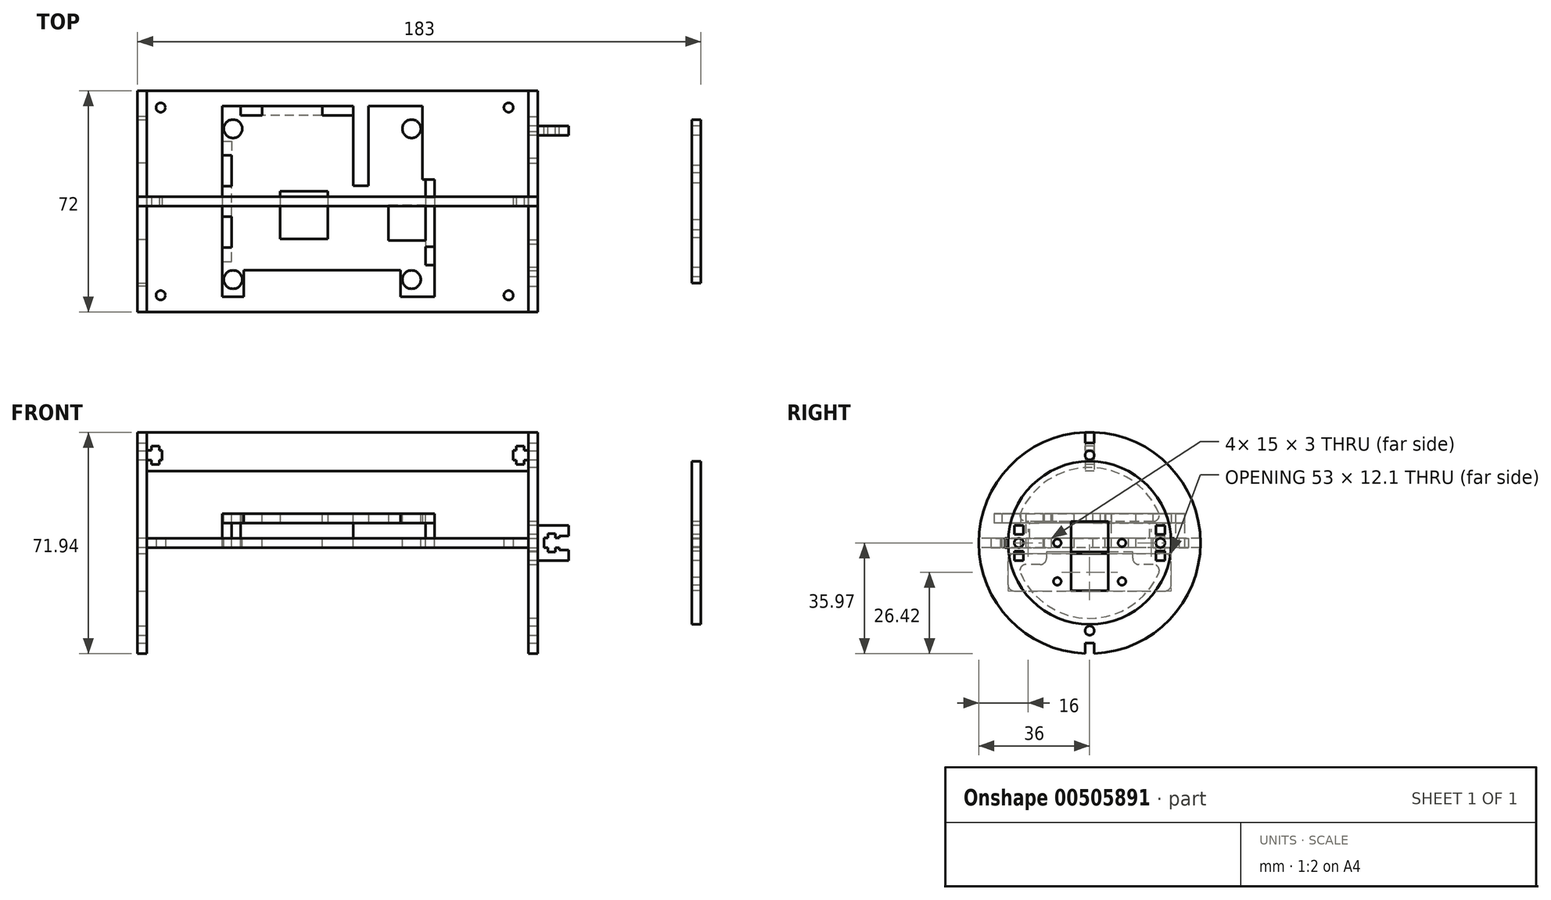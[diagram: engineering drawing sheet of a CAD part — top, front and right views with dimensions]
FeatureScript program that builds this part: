
annotation { "Feature Type Name" : "Feature", "Feature Type Description" : "" }
export const myFeature = defineFeature(function(context is Context, id is Id, definition is map)
    precondition{}
    {
        {
            var Q0;
            Q0=qCreatedBy(makeId("Top.planeOp"),FACE);
            var sketch = newSketch(context, id + "F0", { "sketchPlane" : qUnion([Q0])});
            skLineSegment(sketch, "E0.bottom", {"start": v(-62, 36) * mm, "end": v(62, 36) * mm});
            skLineSegment(sketch, "E0.top", {"start": v(-62, -36) * mm, "end": v(62, -36) * mm});
            skLineSegment(sketch, "E0.left", {"start": v(-62, 36) * mm, "end": v(-62, -36) * mm});
            skLineSegment(sketch, "E0.right", {"start": v(62, 36) * mm, "end": v(62, -36) * mm});
            skPoint(sketch, "E0.middle", {"position": v(0, 0) * mm});
            skLineSegment(sketch, "E1", {"start": v(0, 22.73) * mm, "end": v(0, 0) * mm, "construction": true});
            skLineSegment(sketch, "E2", {"start": v(0, 0) * mm, "end": v(28.2, 0) * mm, "construction": true});
            skLineSegment(sketch, "E3.bottom", {"start": v(62, 27.5) * mm, "end": v(65, 27.5) * mm});
            skLineSegment(sketch, "E3.top", {"start": v(62, 12.5) * mm, "end": v(65, 12.5) * mm});
            skLineSegment(sketch, "E3.left", {"start": v(62, 27.5) * mm, "end": v(62, 12.5) * mm});
            skLineSegment(sketch, "E3.right", {"start": v(65, 27.5) * mm, "end": v(65, 12.5) * mm});
            skPoint(sketch, "E3.middle", {"position": v(63.5, 20) * mm});
            skLineSegment(sketch, "E4.MirrorCS", {"start": v(-62, 27.5) * mm, "end": v(-65, 27.5) * mm});
            skLineSegment(sketch, "E5.MirrorCS", {"start": v(-65, 27.5) * mm, "end": v(-65, 12.5) * mm});
            skLineSegment(sketch, "E6.MirrorCS", {"start": v(-62, 12.5) * mm, "end": v(-65, 12.5) * mm});
            skLineSegment(sketch, "E7.MirrorCS", {"start": v(-62, -27.5) * mm, "end": v(-65, -27.5) * mm});
            skLineSegment(sketch, "E8.MirrorCS", {"start": v(-65, -27.5) * mm, "end": v(-65, -12.5) * mm});
            skLineSegment(sketch, "E9.MirrorCS", {"start": v(-62, -12.5) * mm, "end": v(-65, -12.5) * mm});
            skLineSegment(sketch, "E10.MirrorCS", {"start": v(62, -27.5) * mm, "end": v(65, -27.5) * mm});
            skLineSegment(sketch, "E11.MirrorCS", {"start": v(65, -27.5) * mm, "end": v(65, -12.5) * mm});
            skLineSegment(sketch, "E12.MirrorCS", {"start": v(62, -12.5) * mm, "end": v(65, -12.5) * mm});
            skSolve(sketch);
        }
        {
            var Q0;
            Q0 = qSketchRegion(id + "F0", true);
            extrude(context, id + "F1", {"entities" : qUnion([Q0]), "depth" : 3 * mm});
        }
        {
            var Q0;
            Q0=makeQuery(id+"F1.opExtrude","CAP_FACE",FACE,{"disambiguationData":[OSD([sQuery(id+"F0.wireOp",EDGE,"E0.bottom"),sQuery(id+"F0.wireOp",EDGE,"E0.top"),sQuery(id+"F0.wireOp",EDGE,"E0.left"),sQuery(id+"F0.wireOp",EDGE,"E0.right"),sQuery(id+"F0.wireOp",EDGE,"E3.bottom"),sQuery(id+"F0.wireOp",EDGE,"E3.top"),sQuery(id+"F0.wireOp",EDGE,"E3.right"),sQuery(id+"F0.wireOp",EDGE,"E4.MirrorCS"),sQuery(id+"F0.wireOp",EDGE,"E5.MirrorCS"),sQuery(id+"F0.wireOp",EDGE,"E6.MirrorCS"),sQuery(id+"F0.wireOp",EDGE,"E7.MirrorCS"),sQuery(id+"F0.wireOp",EDGE,"E8.MirrorCS"),sQuery(id+"F0.wireOp",EDGE,"E9.MirrorCS"),sQuery(id+"F0.wireOp",EDGE,"E10.MirrorCS"),sQuery(id+"F0.wireOp",EDGE,"E11.MirrorCS"),sQuery(id+"F0.wireOp",EDGE,"E12.MirrorCS")])],"isStart":true});
            cPlane(context, id + "F2", {"entities" : qUnion([Q0]), "cplaneType" : CPlaneType.OFFSET, "offset" : 8 * mm, "oppositeDirection" : true, "width" : 150 * mm, "height" : 150 * mm});
        }
        {
            var Q0;
            Q0=qCreatedBy(id+"F2.planeOp",FACE);
            var sketch = newSketch(context, id + "F3", { "sketchPlane" : qUnion([Q0])});
            skLineSegment(sketch, "E13.bottom", {"start": v(-37.5, -31) * mm, "end": v(47.5, -31) * mm});
            skLineSegment(sketch, "E13.top", {"start": v(-37.5, 31) * mm, "end": v(47.5, 31) * mm});
            skLineSegment(sketch, "E13.left", {"start": v(-37.5, -31) * mm, "end": v(-37.5, 31) * mm});
            skLineSegment(sketch, "E13.right", {"start": v(47.5, -31) * mm, "end": v(47.5, 31) * mm});
            skPoint(sketch, "E13.middle", {"position": v(5, 0) * mm});
            skLineSegment(sketch, "E14", {"start": v(27.5, -31) * mm, "end": v(27.5, -7.1) * mm});
            skLineSegment(sketch, "E15", {"start": v(27.5, -7.1) * mm, "end": v(31.5, -7.1) * mm});
            skLineSegment(sketch, "E16", {"start": v(31.5, -7.1) * mm, "end": v(31.5, 31) * mm});
            skLineSegment(sketch, "E17.bottom", {"start": v(-18.75, -3.35) * mm, "end": v(-3.25, -3.35) * mm});
            skLineSegment(sketch, "E17.top", {"start": v(-18.75, 12.15) * mm, "end": v(-3.25, 12.15) * mm});
            skLineSegment(sketch, "E17.left", {"start": v(-18.75, -3.35) * mm, "end": v(-18.75, 12.15) * mm});
            skLineSegment(sketch, "E17.right", {"start": v(-3.25, -3.35) * mm, "end": v(-3.25, 12.15) * mm});
            skPoint(sketch, "E17.middle", {"position": v(-11, 4.4) * mm});
            skLineSegment(sketch, "E18.bottom", {"start": v(16.5, 1.15) * mm, "end": v(28.5, 1.15) * mm});
            skLineSegment(sketch, "E18.top", {"start": v(16.5, 12.65) * mm, "end": v(28.5, 12.65) * mm});
            skLineSegment(sketch, "E18.left", {"start": v(16.5, 1.15) * mm, "end": v(16.5, 12.65) * mm});
            skLineSegment(sketch, "E18.right", {"start": v(28.5, 1.15) * mm, "end": v(28.5, 12.65) * mm});
            skLineSegment(sketch, "E19", {"start": v(-37.5, -27.1) * mm, "end": v(47.5, -27.1) * mm, "construction": true});
            skLineSegment(sketch, "E20", {"start": v(-37.5, 28.9) * mm, "end": v(47.5, 28.9) * mm, "construction": true});
            skLineSegment(sketch, "E21", {"start": v(-30.55, 31) * mm, "end": v(-30.55, 22.4) * mm});
            skLineSegment(sketch, "E22", {"start": v(-30.55, 22.4) * mm, "end": v(20.45, 22.4) * mm});
            skLineSegment(sketch, "E23", {"start": v(20.45, 22.4) * mm, "end": v(20.45, 31) * mm});
            skLineSegment(sketch, "E24", {"start": v(5, -31) * mm, "end": v(5, -5.1) * mm});
            skLineSegment(sketch, "E25", {"start": v(5, -5.1) * mm, "end": v(10, -5.1) * mm});
            skLineSegment(sketch, "E26", {"start": v(10, -5.1) * mm, "end": v(10, -31) * mm});
            skCircle(sketch, "E27", {"center": v(-34, -23.6) * mm, "radius": 1.5 * mm});
            skCircle(sketch, "E28", {"center": v(24, -23.6) * mm, "radius": 1.5 * mm});
            skCircle(sketch, "E29", {"center": v(-34, 25.4) * mm, "radius": 1.5 * mm});
            skCircle(sketch, "E30", {"center": v(24, 25.4) * mm, "radius": 1.5 * mm});
            skSolve(sketch);
        }
        {
            var Q0;
            {var subQ6=sQuery(id+"F3.wireOp",EDGE,"E13.left");Q0=makeQuery(id+"F3.imprint","IMPRINT",FACE,{"disambiguationData":[TD([[makeQuery(id+"F3.imprint","IMPRINT",EDGE,{"derivedFrom":subQ6}),-1.0]])]});}
            extrude(context, id + "F4", {"entities" : qUnion([Q0]), "oppositeDirection" : true, "depth" : 3 * mm});
        }
        {
            var Q0;
            Q0=makeQuery(id+"F4.opExtrude","CAP_FACE",FACE,{"disambiguationData":[OSD([sQuery(id+"F3.wireOp",EDGE,"E13.bottom"),sQuery(id+"F3.wireOp",EDGE,"E13.top"),sQuery(id+"F3.wireOp",EDGE,"E13.left"),sQuery(id+"F3.wireOp",EDGE,"E14"),sQuery(id+"F3.wireOp",EDGE,"E15"),sQuery(id+"F3.wireOp",EDGE,"E16"),sQuery(id+"F3.wireOp",EDGE,"E17.bottom"),sQuery(id+"F3.wireOp",EDGE,"E17.top"),sQuery(id+"F3.wireOp",EDGE,"E17.left"),sQuery(id+"F3.wireOp",EDGE,"E17.right"),sQuery(id+"F3.wireOp",EDGE,"E18.bottom"),sQuery(id+"F3.wireOp",EDGE,"E18.top"),sQuery(id+"F3.wireOp",EDGE,"E18.left"),sQuery(id+"F3.wireOp",EDGE,"E18.right"),sQuery(id+"F3.wireOp",EDGE,"E21"),sQuery(id+"F3.wireOp",EDGE,"E22"),sQuery(id+"F3.wireOp",EDGE,"E23"),sQuery(id+"F3.wireOp",EDGE,"E24"),sQuery(id+"F3.wireOp",EDGE,"E25"),sQuery(id+"F3.wireOp",EDGE,"E26"),sQuery(id+"F3.wireOp",EDGE,"E27"),sQuery(id+"F3.wireOp",EDGE,"E28"),sQuery(id+"F3.wireOp",EDGE,"E29"),sQuery(id+"F3.wireOp",EDGE,"E30")])],"isStart":false});
            var sketch = newSketch(context, id + "F5", { "sketchPlane" : qUnion([Q0])});
            skLineSegment(sketch, "E31.bottom", {"start": v(31.5, -20.68) * mm, "end": v(28.5, -20.68) * mm});
            skLineSegment(sketch, "E31.top", {"start": v(31.5, -14.68) * mm, "end": v(28.5, -14.68) * mm});
            skLineSegment(sketch, "E31.left", {"start": v(31.5, -20.68) * mm, "end": v(31.5, -14.68) * mm});
            skLineSegment(sketch, "E31.right", {"start": v(28.5, -20.68) * mm, "end": v(28.5, -14.68) * mm});
            skPoint(sketch, "E31.middle", {"position": v(30, -17.68) * mm});
            skLineSegment(sketch, "E32.bottom", {"start": v(31.5, 7.1) * mm, "end": v(28.5, 7.1) * mm});
            skLineSegment(sketch, "E32.top", {"start": v(31.5, 1.1) * mm, "end": v(28.5, 1.1) * mm});
            skLineSegment(sketch, "E32.left", {"start": v(31.5, 7.1) * mm, "end": v(31.5, 1.1) * mm});
            skLineSegment(sketch, "E32.right", {"start": v(28.5, 7.1) * mm, "end": v(28.5, 1.1) * mm});
            skPoint(sketch, "E32.middle", {"position": v(30, 4.1) * mm});
            skLineSegment(sketch, "E33.bottom", {"start": v(5, 31) * mm, "end": v(-5, 31) * mm});
            skLineSegment(sketch, "E33.top", {"start": v(5, 28) * mm, "end": v(-5, 28) * mm});
            skLineSegment(sketch, "E33.left", {"start": v(5, 31) * mm, "end": v(5, 28) * mm});
            skLineSegment(sketch, "E33.right", {"start": v(-5, 31) * mm, "end": v(-5, 28) * mm});
            skPoint(sketch, "E33.middle", {"position": v(0, 29.5) * mm});
            skLineSegment(sketch, "E34.bottom", {"start": v(-24.5, 31) * mm, "end": v(-31.5, 31) * mm});
            skLineSegment(sketch, "E34.top", {"start": v(-24.5, 28) * mm, "end": v(-31.5, 28) * mm});
            skLineSegment(sketch, "E34.left", {"start": v(-24.5, 31) * mm, "end": v(-24.5, 28) * mm});
            skLineSegment(sketch, "E34.right", {"start": v(-31.5, 31) * mm, "end": v(-31.5, 28) * mm});
            skPoint(sketch, "E34.middle", {"position": v(-28, 29.5) * mm});
            skLineSegment(sketch, "E35.bottom", {"start": v(-37.5, -15) * mm, "end": v(-34.5, -15) * mm});
            skLineSegment(sketch, "E35.top", {"start": v(-37.5, -5) * mm, "end": v(-34.5, -5) * mm});
            skLineSegment(sketch, "E35.left", {"start": v(-37.5, -15) * mm, "end": v(-37.5, -5) * mm});
            skLineSegment(sketch, "E35.right", {"start": v(-34.5, -15) * mm, "end": v(-34.5, -5) * mm});
            skPoint(sketch, "E35.middle", {"position": v(-36, -10) * mm});
            skLineSegment(sketch, "E36.bottom", {"start": v(-37.5, 5) * mm, "end": v(-34.5, 5) * mm});
            skLineSegment(sketch, "E36.top", {"start": v(-37.5, 15) * mm, "end": v(-34.5, 15) * mm});
            skLineSegment(sketch, "E36.left", {"start": v(-37.5, 5) * mm, "end": v(-37.5, 15) * mm});
            skLineSegment(sketch, "E36.right", {"start": v(-34.5, 5) * mm, "end": v(-34.5, 15) * mm});
            skPoint(sketch, "E36.middle", {"position": v(-36, 10) * mm});
            skPoint(sketch, "E37", {"position": v(-37.5, 0) * mm});
            skCircle(sketch, "E38.0", {"center": v(24, -25.4) * mm, "radius": 1.5 * mm, "construction": true});
            skCircle(sketch, "E38.1", {"center": v(24, 23.6) * mm, "radius": 1.5 * mm, "construction": true});
            skCircle(sketch, "E38.2", {"center": v(-34, 23.6) * mm, "radius": 1.5 * mm, "construction": true});
            skCircle(sketch, "E38.3", {"center": v(-34, -25.4) * mm, "radius": 1.5 * mm, "construction": true});
            skCircle(sketch, "E39", {"center": v(24, -25.4) * mm, "radius": 3 * mm});
            skCircle(sketch, "E40", {"center": v(-34, -25.4) * mm, "radius": 3 * mm});
            skCircle(sketch, "E41", {"center": v(24, 23.6) * mm, "radius": 3 * mm});
            skCircle(sketch, "E42", {"center": v(-34, 23.6) * mm, "radius": 3 * mm});
            skSolve(sketch);
        }
        {
            var Q0;
            Q0=makeQuery(id+"F5.imprint","IMPRINT",FACE,{"disambiguationData":[TD([[makeQuery(id+"F5.imprint","IMPRINT",EDGE,{"derivedFrom":sQuery(id+"F5.wireOp",EDGE,"E31.bottom")}),-1.0]])]});
            var Q1;
            Q1=makeQuery(id+"F5.imprint","IMPRINT",FACE,{"disambiguationData":[TD([[makeQuery(id+"F5.imprint","IMPRINT",EDGE,{"derivedFrom":sQuery(id+"F5.wireOp",EDGE,"E32.bottom")}),-1.0]])]});
            var Q2;
            Q2=makeQuery(id+"F5.imprint","IMPRINT",FACE,{"disambiguationData":[TD([[makeQuery(id+"F5.imprint","IMPRINT",EDGE,{"derivedFrom":sQuery(id+"F5.wireOp",EDGE,"E33.bottom")}),-1.0]])]});
            var Q3;
            Q3=makeQuery(id+"F5.imprint","IMPRINT",FACE,{"disambiguationData":[TD([[makeQuery(id+"F5.imprint","IMPRINT",EDGE,{"derivedFrom":sQuery(id+"F5.wireOp",EDGE,"E34.bottom")}),-1.0]])]});
            var Q4;
            Q4=makeQuery(id+"F5.imprint","IMPRINT",FACE,{"disambiguationData":[TD([[makeQuery(id+"F5.imprint","IMPRINT",EDGE,{"derivedFrom":sQuery(id+"F5.wireOp",EDGE,"E36.bottom")}),1.0]])]});
            var Q5;
            Q5=makeQuery(id+"F5.imprint","IMPRINT",FACE,{"disambiguationData":[TD([[makeQuery(id+"F5.imprint","IMPRINT",EDGE,{"derivedFrom":sQuery(id+"F5.wireOp",EDGE,"E35.bottom")}),1.0]])]});
            extrude(context, id + "F6", {"entities" : qUnion([Q0, Q1, Q2, Q3, Q4, Q5]), "operationType" : NewBodyOperationType.REMOVE, "oppositeDirection" : true, "depth" : 25 * mm});
        }
        {
            var Q0;
            Q0=makeQuery(id+"F5.imprint","IMPRINT",FACE,{"disambiguationData":[TD([[makeQuery(id+"F5.imprint","IMPRINT",EDGE,{"derivedFrom":sQuery(id+"F5.wireOp",EDGE,"E39")}),1.0]])]});
            var Q1;
            Q1=makeQuery(id+"F5.imprint","IMPRINT",FACE,{"disambiguationData":[TD([[makeQuery(id+"F5.imprint","IMPRINT",EDGE,{"derivedFrom":makeQuery(id+"F4.opExtrude","CAP_EDGE",EDGE,{"disambiguationData":[OSD([sQuery(id+"F3.wireOp",EDGE,"E30")])],"isStart":false})}),-1.0]])]});
            var Q2;
            Q2=makeQuery(id+"F5.imprint","IMPRINT",FACE,{"disambiguationData":[TD([[makeQuery(id+"F5.imprint","IMPRINT",EDGE,{"derivedFrom":sQuery(id+"F5.wireOp",EDGE,"E40")}),1.0]])]});
            var Q3;
            Q3=makeQuery(id+"F5.imprint","IMPRINT",FACE,{"disambiguationData":[TD([[makeQuery(id+"F5.imprint","IMPRINT",EDGE,{"derivedFrom":makeQuery(id+"F4.opExtrude","CAP_EDGE",EDGE,{"disambiguationData":[OSD([sQuery(id+"F3.wireOp",EDGE,"E29")])],"isStart":false})}),-1.0]])]});
            var Q4;
            Q4=makeQuery(id+"F5.imprint","IMPRINT",FACE,{"disambiguationData":[TD([[makeQuery(id+"F5.imprint","IMPRINT",EDGE,{"derivedFrom":sQuery(id+"F5.wireOp",EDGE,"E41")}),1.0]])]});
            var Q5;
            Q5=makeQuery(id+"F5.imprint","IMPRINT",FACE,{"disambiguationData":[TD([[makeQuery(id+"F5.imprint","IMPRINT",EDGE,{"derivedFrom":makeQuery(id+"F4.opExtrude","CAP_EDGE",EDGE,{"disambiguationData":[OSD([sQuery(id+"F3.wireOp",EDGE,"E28")])],"isStart":false})}),-1.0]])]});
            var Q6;
            Q6=makeQuery(id+"F5.imprint","IMPRINT",FACE,{"disambiguationData":[TD([[makeQuery(id+"F5.imprint","IMPRINT",EDGE,{"derivedFrom":sQuery(id+"F5.wireOp",EDGE,"E42")}),1.0]])]});
            var Q7;
            Q7=makeQuery(id+"F5.imprint","IMPRINT",FACE,{"disambiguationData":[TD([[makeQuery(id+"F5.imprint","IMPRINT",EDGE,{"derivedFrom":makeQuery(id+"F4.opExtrude","CAP_EDGE",EDGE,{"disambiguationData":[OSD([sQuery(id+"F3.wireOp",EDGE,"E27")])],"isStart":false})}),-1.0]])]});
            extrude(context, id + "F7", {"entities" : qUnion([Q0, Q1, Q2, Q3, Q4, Q5, Q6, Q7]), "operationType" : NewBodyOperationType.REMOVE, "oppositeDirection" : true, "depth" : 25 * mm});
        }
        {
            var Q0;
            {var subQ0=sQuery(id+"F3.wireOp",EDGE,"E30");var subQ1=sQuery(id+"F3.wireOp",EDGE,"E29");var subQ2=sQuery(id+"F3.wireOp",EDGE,"E28");var subQ3=sQuery(id+"F3.wireOp",EDGE,"E27");var subQ4=sQuery(id+"F3.wireOp",EDGE,"E26");var subQ5=sQuery(id+"F3.wireOp",EDGE,"E25");var subQ6=sQuery(id+"F3.wireOp",EDGE,"E24");var subQ7=sQuery(id+"F3.wireOp",EDGE,"E23");var subQ8=sQuery(id+"F3.wireOp",EDGE,"E22");var subQ9=sQuery(id+"F3.wireOp",EDGE,"E21");var subQ10=sQuery(id+"F3.wireOp",EDGE,"E18.right");var subQ11=sQuery(id+"F3.wireOp",EDGE,"E18.left");var subQ12=sQuery(id+"F3.wireOp",EDGE,"E18.top");var subQ13=sQuery(id+"F3.wireOp",EDGE,"E18.bottom");var subQ14=sQuery(id+"F3.wireOp",EDGE,"E17.right");var subQ15=sQuery(id+"F3.wireOp",EDGE,"E17.left");var subQ16=sQuery(id+"F3.wireOp",EDGE,"E17.top");var subQ17=sQuery(id+"F3.wireOp",EDGE,"E17.bottom");var subQ18=sQuery(id+"F3.wireOp",EDGE,"E16");var subQ19=sQuery(id+"F3.wireOp",EDGE,"E15");var subQ20=sQuery(id+"F3.wireOp",EDGE,"E14");var subQ21=sQuery(id+"F3.wireOp",EDGE,"E13.left");var subQ22=sQuery(id+"F3.wireOp",EDGE,"E13.top");var subQ23=sQuery(id+"F3.wireOp",EDGE,"E13.bottom");Q0=makeQuery(id+"F6.boolean.opBoolean","COPY",FACE,{"disambiguationData":[TD([makeQuery(id+"F4.opExtrude","CAP_FACE",FACE,{"disambiguationData":[OSD([subQ23,subQ22,subQ21,subQ20,subQ19,subQ18,subQ17,subQ16,subQ15,subQ14,subQ13,subQ12,subQ11,subQ10,subQ9,subQ8,subQ7,subQ6,subQ5,subQ4,subQ3,subQ2,subQ1,subQ0])],"isStart":true})])],"derivedFrom":makeQuery(id+"F6.opExtrude","SWEPT_FACE",FACE,{"disambiguationData":[OSD([sQuery(id+"F5.wireOp",EDGE,"E35.right")])]})});}
            var sketch = newSketch(context, id + "F8", { "sketchPlane" : qUnion([Q0])});
            skLineSegment(sketch, "E43.0", {"start": v(15, 0) * mm, "end": v(15, 3) * mm});
            skLineSegment(sketch, "E43.1", {"start": v(15, 0) * mm, "end": v(5, 0) * mm});
            skLineSegment(sketch, "E43.2", {"start": v(5, 0) * mm, "end": v(5, 3) * mm});
            skLineSegment(sketch, "E43.3", {"start": v(5, 8) * mm, "end": v(5, 11) * mm});
            skLineSegment(sketch, "E43.4", {"start": v(15, 11) * mm, "end": v(5, 11) * mm});
            skLineSegment(sketch, "E43.5", {"start": v(15, 8) * mm, "end": v(15, 11) * mm});
            skLineSegment(sketch, "E43.6", {"start": v(-5, 0) * mm, "end": v(-5, 3) * mm});
            skLineSegment(sketch, "E43.7", {"start": v(-5, 8) * mm, "end": v(-5, 11) * mm});
            skLineSegment(sketch, "E43.8", {"start": v(-5, 11) * mm, "end": v(-15, 11) * mm});
            skLineSegment(sketch, "E43.9", {"start": v(-15, 8) * mm, "end": v(-15, 11) * mm});
            skLineSegment(sketch, "E43.10", {"start": v(-15, 0) * mm, "end": v(-15, 3) * mm});
            skLineSegment(sketch, "E43.11", {"start": v(-5, 0) * mm, "end": v(-15, 0) * mm});
            skLineSegment(sketch, "E44", {"start": v(5, 3) * mm, "end": v(-5, 3) * mm});
            skLineSegment(sketch, "E45", {"start": v(5, 8) * mm, "end": v(-5, 8) * mm});
            skLineSegment(sketch, "E46", {"start": v(15, 3) * mm, "end": v(19.5, 3) * mm});
            skLineSegment(sketch, "E47", {"start": v(19.5, 3) * mm, "end": v(19.5, 8) * mm});
            skLineSegment(sketch, "E48", {"start": v(19.5, 8) * mm, "end": v(15, 8) * mm});
            skLineSegment(sketch, "E49", {"start": v(-15, 3) * mm, "end": v(-19.5, 3) * mm});
            skLineSegment(sketch, "E50", {"start": v(-19.5, 3) * mm, "end": v(-19.5, 8) * mm});
            skLineSegment(sketch, "E51", {"start": v(-19.5, 8) * mm, "end": v(-15, 8) * mm});
            skSolve(sketch);
        }
        {
            var Q0;
            Q0 = qSketchRegion(id + "F8", true);
            extrude(context, id + "F9", {"entities" : qUnion([Q0]), "depth" : 3 * mm});
        }
        {
            var Q0;
            {var subQ6=sQuery(id+"F3.wireOp",EDGE,"E24");Q0=makeQuery(id+"F6.boolean.opBoolean","COPY",FACE,{"disambiguationData":[TD([makeQuery(id+"F4.opExtrude","SWEPT_FACE",FACE,{"disambiguationData":[OSD([subQ6])]})])],"derivedFrom":makeQuery(id+"F6.opExtrude","SWEPT_FACE",FACE,{"disambiguationData":[OSD([sQuery(id+"F5.wireOp",EDGE,"E33.top")])]})});}
            var sketch = newSketch(context, id + "F10", { "sketchPlane" : qUnion([Q0])});
            skLineSegment(sketch, "E52.0", {"start": v(-5, 11) * mm, "end": v(5, 11) * mm});
            skLineSegment(sketch, "E52.1", {"start": v(5, 8) * mm, "end": v(5, 11) * mm});
            skLineSegment(sketch, "E52.2", {"start": v(24.5, 8) * mm, "end": v(24.5, 11) * mm});
            skLineSegment(sketch, "E52.3", {"start": v(24.5, 11) * mm, "end": v(31.5, 11) * mm});
            skLineSegment(sketch, "E52.4", {"start": v(24.5, 0) * mm, "end": v(31.5, 0) * mm});
            skLineSegment(sketch, "E52.5", {"start": v(24.5, 0) * mm, "end": v(24.5, 3) * mm});
            skLineSegment(sketch, "E52.6", {"start": v(-5, 0) * mm, "end": v(5, 0) * mm});
            skLineSegment(sketch, "E52.7", {"start": v(5, 0) * mm, "end": v(5, 3) * mm});
            skLineSegment(sketch, "E53", {"start": v(-5, 11) * mm, "end": v(-5, 0) * mm});
            skLineSegment(sketch, "E54", {"start": v(31.5, 11) * mm, "end": v(31.5, 0) * mm});
            skLineSegment(sketch, "E55", {"start": v(24.5, 8) * mm, "end": v(5, 8) * mm});
            skLineSegment(sketch, "E56", {"start": v(5, 3) * mm, "end": v(24.5, 3) * mm});
            skSolve(sketch);
        }
        {
            var Q0;
            Q0 = qSketchRegion(id + "F10", true);
            extrude(context, id + "F11", {"entities" : qUnion([Q0]), "depth" : 3 * mm});
        }
        {
            var Q0;
            {var subQ19=sQuery(id+"F3.wireOp",EDGE,"E15");Q0=makeQuery(id+"F6.boolean.opBoolean","COPY",FACE,{"disambiguationData":[TD([makeQuery(id+"F4.opExtrude","SWEPT_FACE",FACE,{"disambiguationData":[OSD([subQ19])]})])],"derivedFrom":makeQuery(id+"F6.opExtrude","SWEPT_FACE",FACE,{"disambiguationData":[OSD([sQuery(id+"F5.wireOp",EDGE,"E32.right")])]})});}
            var sketch = newSketch(context, id + "F12", { "sketchPlane" : qUnion([Q0])});
            skLineSegment(sketch, "E57.0", {"start": v(7.1, 11) * mm, "end": v(1.1, 11) * mm});
            skLineSegment(sketch, "E57.1", {"start": v(1.1, 8) * mm, "end": v(1.1, 11) * mm});
            skLineSegment(sketch, "E57.2", {"start": v(-14.68, 8) * mm, "end": v(-14.68, 11) * mm});
            skLineSegment(sketch, "E57.3", {"start": v(-20.68, 11) * mm, "end": v(-14.68, 11) * mm});
            skLineSegment(sketch, "E57.4", {"start": v(-20.68, 0) * mm, "end": v(-14.68, 0) * mm});
            skLineSegment(sketch, "E57.5", {"start": v(-14.68, 0) * mm, "end": v(-14.68, 3) * mm});
            skLineSegment(sketch, "E57.6", {"start": v(7.1, 0) * mm, "end": v(1.1, 0) * mm});
            skLineSegment(sketch, "E57.7", {"start": v(1.1, 0) * mm, "end": v(1.1, 3) * mm});
            skLineSegment(sketch, "E58", {"start": v(1.1, 3) * mm, "end": v(-14.68, 3) * mm});
            skLineSegment(sketch, "E59", {"start": v(1.1, 8) * mm, "end": v(-14.68, 8) * mm});
            skLineSegment(sketch, "E60", {"start": v(7.1, 0) * mm, "end": v(7.1, 11) * mm});
            skLineSegment(sketch, "E61", {"start": v(-20.68, 0) * mm, "end": v(-20.68, 11) * mm});
            skSolve(sketch);
        }
        {
            var Q0;
            Q0 = qSketchRegion(id + "F12", true);
            extrude(context, id + "F13", {"entities" : qUnion([Q0]), "depth" : 3 * mm});
        }
        {
            var Q0;
            {var subQ0=sQuery(id+"F0.wireOp",EDGE,"E0.right");Q0=makeQuery(id+"F1.opExtrude","SWEPT_FACE",FACE,{"disambiguationData":[OSD([subQ0]),TDD([makeQuery(id+"F0.imprint","IMPRINT",EDGE,{"disambiguationData":[TD([[makeQuery(id+"F0.imprint","INTERSECT",VERTEX,{"derivedFrom":[subQ0,sQuery(id+"F0.wireOp",EDGE,"E12.MirrorCS")]}),1.0]])],"derivedFrom":subQ0})])]});}
            var sketch = newSketch(context, id + "F14", { "sketchPlane" : qUnion([Q0])});
            skLineSegment(sketch, "E62", {"start": v(0, 0) * mm, "end": v(0, 3) * mm, "construction": true});
            skPoint(sketch, "E63", {"position": v(0, 1.5) * mm});
            skCircle(sketch, "E64", {"center": v(0, 1.5) * mm, "radius": 36 * mm});
            skCircle(sketch, "E65", {"center": v(0, 1.5) * mm, "radius": 24.5 * mm});
            skLineSegment(sketch, "E66", {"start": v(23.48, -5.5) * mm, "end": v(-23.48, -5.5) * mm});
            skLineSegment(sketch, "E67", {"start": v(23.48, 8.5) * mm, "end": v(-23.48, 8.5) * mm});
            skLineSegment(sketch, "E68", {"start": v(0, 1.5) * mm, "end": v(0, -10.66) * mm, "construction": true});
            skLineSegment(sketch, "E69", {"start": v(0, 1.5) * mm, "end": v(-8.88, 1.5) * mm, "construction": true});
            skLineSegment(sketch, "E70.bottom", {"start": v(24.5, -4.25) * mm, "end": v(21.5, -4.25) * mm});
            skLineSegment(sketch, "E70.top", {"start": v(24.5, -1.25) * mm, "end": v(21.5, -1.25) * mm});
            skLineSegment(sketch, "E70.left", {"start": v(24.5, -4.25) * mm, "end": v(24.5, -1.25) * mm});
            skLineSegment(sketch, "E70.right", {"start": v(21.5, -4.25) * mm, "end": v(21.5, -1.25) * mm});
            skPoint(sketch, "E70.middle", {"position": v(23, -2.75) * mm});
            skLineSegment(sketch, "E71.MirrorCS", {"start": v(21.5, 7.25) * mm, "end": v(21.5, 4.25) * mm});
            skLineSegment(sketch, "E72.MirrorCS", {"start": v(24.5, 7.25) * mm, "end": v(21.5, 7.25) * mm});
            skLineSegment(sketch, "E73.MirrorCS", {"start": v(24.5, 7.25) * mm, "end": v(24.5, 4.25) * mm});
            skLineSegment(sketch, "E74.MirrorCS", {"start": v(24.5, 4.25) * mm, "end": v(21.5, 4.25) * mm});
            skPoint(sketch, "E75.MirrorP", {"position": v(23, 5.75) * mm});
            skLineSegment(sketch, "E76.MirrorCS", {"start": v(-21.5, -4.25) * mm, "end": v(-21.5, -1.25) * mm});
            skLineSegment(sketch, "E77.MirrorCS", {"start": v(-24.5, -4.25) * mm, "end": v(-21.5, -4.25) * mm});
            skLineSegment(sketch, "E78.MirrorCS", {"start": v(-24.5, -4.25) * mm, "end": v(-24.5, -1.25) * mm});
            skLineSegment(sketch, "E79.MirrorCS", {"start": v(-24.5, -1.25) * mm, "end": v(-21.5, -1.25) * mm});
            skLineSegment(sketch, "E80.MirrorCS", {"start": v(-24.5, 4.25) * mm, "end": v(-21.5, 4.25) * mm});
            skLineSegment(sketch, "E81.MirrorCS", {"start": v(-21.5, 7.25) * mm, "end": v(-21.5, 4.25) * mm});
            skLineSegment(sketch, "E82.MirrorCS", {"start": v(-24.5, 7.25) * mm, "end": v(-21.5, 7.25) * mm});
            skLineSegment(sketch, "E83.MirrorCS", {"start": v(-24.5, 7.25) * mm, "end": v(-24.5, 4.25) * mm});
            skLineSegment(sketch, "E84", {"start": v(14, -5.5) * mm, "end": v(14, -1.5) * mm});
            skLineSegment(sketch, "E85", {"start": v(14, -1.5) * mm, "end": v(-14, -1.5) * mm});
            skLineSegment(sketch, "E86", {"start": v(-14, -1.5) * mm, "end": v(-14, -5.5) * mm});
            skPoint(sketch, "E87", {"position": v(0, -1.5) * mm});
            skLineSegment(sketch, "E88.0.0", {"start": v(12.5, 0) * mm, "end": v(27.5, 0) * mm});
            skLineSegment(sketch, "E88.0.1", {"start": v(27.5, 0) * mm, "end": v(27.5, 3) * mm});
            skLineSegment(sketch, "E88.0.2", {"start": v(27.5, 3) * mm, "end": v(12.5, 3) * mm});
            skLineSegment(sketch, "E88.0.3", {"start": v(12.5, 3) * mm, "end": v(12.5, 0) * mm});
            skLineSegment(sketch, "E88.1.0", {"start": v(-27.5, 0) * mm, "end": v(-12.5, 0) * mm});
            skLineSegment(sketch, "E88.1.1", {"start": v(-12.5, 0) * mm, "end": v(-12.5, 3) * mm});
            skLineSegment(sketch, "E88.1.2", {"start": v(-12.5, 3) * mm, "end": v(-27.5, 3) * mm});
            skLineSegment(sketch, "E88.1.3", {"start": v(-27.5, 3) * mm, "end": v(-27.5, 0) * mm});
            skSolve(sketch);
        }
        {
            var Q0;
            Q0=makeQuery(id+"F14.imprint","IMPRINT",FACE,{"disambiguationData":[TD([[makeQuery(id+"F14.imprint","IMPRINT",EDGE,{"derivedFrom":sQuery(id+"F14.wireOp",EDGE,"E64")}),1.0]])]});
            var Q1;
            {var subQ13=sQuery(id+"F14.wireOp",EDGE,"E70.right");Q1=makeQuery(id+"F14.imprint","IMPRINT",FACE,{"disambiguationData":[TD([[makeQuery(id+"F14.imprint","IMPRINT",EDGE,{"derivedFrom":subQ13}),1.0]])]});}
            var Q2;
            {var subQ5=sQuery(id+"F14.wireOp",EDGE,"E67");Q2=makeQuery(id+"F14.imprint","IMPRINT",FACE,{"disambiguationData":[TD([[makeQuery(id+"F14.imprint","IMPRINT",EDGE,{"derivedFrom":subQ5}),1.0]])]});}
            var Q3;
            Q3=makeQuery(id+"F14.imprint","IMPRINT",FACE,{"disambiguationData":[TD([[makeQuery(id+"F14.imprint","IMPRINT",EDGE,{"derivedFrom":sQuery(id+"F14.wireOp",EDGE,"E88.0.3")}),-1.0]])]});
            extrude(context, id + "F15", {"entities" : qUnion([Q0, Q1, Q2, Q3]), "depth" : 3 * mm});
        }
        {
            var Q0;
            Q0=makeQuery(id+"F15.opExtrude","SWEPT_EDGE",EDGE,{"disambiguationData":[OSD([sQuery(id+"F14.wireOp",EDGE,"E66"),sQuery(id+"F14.wireOp",EDGE,"E84")])]});
            var Q1;
            Q1=makeQuery(id+"F15.opExtrude","SWEPT_EDGE",EDGE,{"disambiguationData":[OSD([sQuery(id+"F14.wireOp",EDGE,"E66"),sQuery(id+"F14.wireOp",EDGE,"E86")])]});
            var Q2;
            {var subQ0=sQuery(id+"F14.wireOp",EDGE,"E66");var subQ1=sQuery(id+"F14.wireOp",EDGE,"E65");Q2=makeQuery(id+"F15.opExtrude","SWEPT_EDGE",EDGE,{"disambiguationData":[OSD([subQ1,subQ0]),TDD([makeQuery(id+"F14.imprint","INTERSECT",VERTEX,{"disambiguationData":[OD(0.0)],"derivedFrom":[subQ1,subQ0]})])]});}
            var Q3;
            {var subQ0=sQuery(id+"F14.wireOp",EDGE,"E66");var subQ1=sQuery(id+"F14.wireOp",EDGE,"E65");Q3=makeQuery(id+"F15.opExtrude","SWEPT_EDGE",EDGE,{"disambiguationData":[OSD([subQ1,subQ0]),TDD([makeQuery(id+"F14.imprint","INTERSECT",VERTEX,{"disambiguationData":[OD(1.0)],"derivedFrom":[subQ1,subQ0]})])]});}
            var Q4;
            {var subQ0=sQuery(id+"F14.wireOp",EDGE,"E67");var subQ1=sQuery(id+"F14.wireOp",EDGE,"E65");Q4=makeQuery(id+"F15.opExtrude","SWEPT_EDGE",EDGE,{"disambiguationData":[OSD([subQ1,subQ0]),TDD([makeQuery(id+"F14.imprint","INTERSECT",VERTEX,{"disambiguationData":[OD(0.0)],"derivedFrom":[subQ1,subQ0]})])]});}
            var Q5;
            {var subQ0=sQuery(id+"F14.wireOp",EDGE,"E67");var subQ1=sQuery(id+"F14.wireOp",EDGE,"E65");Q5=makeQuery(id+"F15.opExtrude","SWEPT_EDGE",EDGE,{"disambiguationData":[OSD([subQ1,subQ0]),TDD([makeQuery(id+"F14.imprint","INTERSECT",VERTEX,{"disambiguationData":[OD(1.0)],"derivedFrom":[subQ1,subQ0]})])]});}
            fillet(context, id + "F16", {"entities" : qUnion([Q0, Q1, Q2, Q3, Q4, Q5]), "radius" : 2 * mm, "tangentPropagation" : true, "allowEdgeOverflow" : false});
        }
        {
            var Q0;
            {var subQ0=sQuery(id+"F0.wireOp",EDGE,"E0.left");Q0=makeQuery(id+"F1.opExtrude","SWEPT_FACE",FACE,{"disambiguationData":[OSD([subQ0]),TDD([makeQuery(id+"F0.imprint","IMPRINT",EDGE,{"disambiguationData":[TD([[makeQuery(id+"F0.imprint","INTERSECT",VERTEX,{"derivedFrom":[subQ0,sQuery(id+"F0.wireOp",EDGE,"E6.MirrorCS")]}),-1.0]])],"derivedFrom":subQ0})])]});}
            var sketch = newSketch(context, id + "F17", { "sketchPlane" : qUnion([Q0])});
            skCircle(sketch, "E89.0", {"center": v(0, 1.5) * mm, "radius": 36 * mm});
            skLineSegment(sketch, "E90.0.0", {"start": v(12.5, 0) * mm, "end": v(27.5, 0) * mm});
            skLineSegment(sketch, "E90.0.1", {"start": v(27.5, 0) * mm, "end": v(27.5, 3) * mm});
            skLineSegment(sketch, "E90.0.2", {"start": v(27.5, 3) * mm, "end": v(12.5, 3) * mm});
            skLineSegment(sketch, "E90.0.3", {"start": v(12.5, 3) * mm, "end": v(12.5, 0) * mm});
            skLineSegment(sketch, "E90.1.0", {"start": v(-27.5, 0) * mm, "end": v(-12.5, 0) * mm});
            skLineSegment(sketch, "E90.1.1", {"start": v(-12.5, 0) * mm, "end": v(-12.5, 3) * mm});
            skLineSegment(sketch, "E90.1.2", {"start": v(-12.5, 3) * mm, "end": v(-27.5, 3) * mm});
            skLineSegment(sketch, "E90.1.3", {"start": v(-27.5, 3) * mm, "end": v(-27.5, 0) * mm});
            skLineSegment(sketch, "E91.bottom", {"start": v(24.5, -14.1) * mm, "end": v(-24.5, -14.1) * mm});
            skLineSegment(sketch, "E91.top", {"start": v(24.5, -2) * mm, "end": v(-24.5, -2) * mm});
            skLineSegment(sketch, "E91.left", {"start": v(26.5, -12.1) * mm, "end": v(26.5, -4) * mm});
            skLineSegment(sketch, "E91.right", {"start": v(-26.5, -12.1) * mm, "end": v(-26.5, -4) * mm});
            skPoint(sketch, "E91.middle", {"position": v(0, -8.05) * mm});
            skPoint(sketch, "E92.visualSharp", {"position": v(26.5, -14.1) * mm});
            skArc(sketch, "E92.filletArc", {"start": v(24.5, -14.1) * mm, "mid": v(25.91, -13.51) * mm, "end": v(26.5, -12.1) * mm});
            skPoint(sketch, "E93.visualSharp", {"position": v(26.5, -2) * mm});
            skArc(sketch, "E93.filletArc", {"start": v(26.5, -4) * mm, "mid": v(25.91, -2.59) * mm, "end": v(24.5, -2) * mm});
            skPoint(sketch, "E94.visualSharp", {"position": v(-26.5, -2) * mm});
            skArc(sketch, "E94.filletArc", {"start": v(-24.5, -2) * mm, "mid": v(-25.91, -2.59) * mm, "end": v(-26.5, -4) * mm});
            skPoint(sketch, "E95.visualSharp", {"position": v(-26.5, -14.1) * mm});
            skArc(sketch, "E95.filletArc", {"start": v(-26.5, -12.1) * mm, "mid": v(-25.91, -13.51) * mm, "end": v(-24.5, -14.1) * mm});
            skSolve(sketch);
        }
        {
            var Q0;
            Q0 = qSketchRegion(id + "F17", true);
            extrude(context, id + "F18", {"entities" : qUnion([Q0]), "depth" : 3 * mm});
        }
        {
            var Q0;
            Q0=makeQuery(id+"F15.opExtrude","CAP_FACE",FACE,{"disambiguationData":[OSD([sQuery(id+"F14.wireOp",EDGE,"E64"),sQuery(id+"F14.wireOp",EDGE,"E65"),sQuery(id+"F14.wireOp",EDGE,"E66"),sQuery(id+"F14.wireOp",EDGE,"E67"),sQuery(id+"F14.wireOp",EDGE,"E70.bottom"),sQuery(id+"F14.wireOp",EDGE,"E70.top"),sQuery(id+"F14.wireOp",EDGE,"E70.left"),sQuery(id+"F14.wireOp",EDGE,"E70.right"),sQuery(id+"F14.wireOp",EDGE,"E71.MirrorCS"),sQuery(id+"F14.wireOp",EDGE,"E72.MirrorCS"),sQuery(id+"F14.wireOp",EDGE,"E73.MirrorCS"),sQuery(id+"F14.wireOp",EDGE,"E74.MirrorCS"),sQuery(id+"F14.wireOp",EDGE,"E76.MirrorCS"),sQuery(id+"F14.wireOp",EDGE,"E77.MirrorCS"),sQuery(id+"F14.wireOp",EDGE,"E78.MirrorCS"),sQuery(id+"F14.wireOp",EDGE,"E79.MirrorCS"),sQuery(id+"F14.wireOp",EDGE,"E80.MirrorCS"),sQuery(id+"F14.wireOp",EDGE,"E81.MirrorCS"),sQuery(id+"F14.wireOp",EDGE,"E82.MirrorCS"),sQuery(id+"F14.wireOp",EDGE,"E83.MirrorCS"),sQuery(id+"F14.wireOp",EDGE,"E84"),sQuery(id+"F14.wireOp",EDGE,"E85"),sQuery(id+"F14.wireOp",EDGE,"E86"),sQuery(id+"F14.wireOp",EDGE,"E88.0.0"),sQuery(id+"F14.wireOp",EDGE,"E88.0.1"),sQuery(id+"F14.wireOp",EDGE,"E88.0.2"),sQuery(id+"F14.wireOp",EDGE,"E88.0.3"),sQuery(id+"F14.wireOp",EDGE,"E88.1.0"),sQuery(id+"F14.wireOp",EDGE,"E88.1.1"),sQuery(id+"F14.wireOp",EDGE,"E88.1.2"),sQuery(id+"F14.wireOp",EDGE,"E88.1.3")])],"isStart":false});
            var sketch = newSketch(context, id + "F19", { "sketchPlane" : qUnion([Q0])});
            skCircle(sketch, "E96", {"center": v(0, -27) * mm, "radius": 1.5 * mm});
            skCircle(sketch, "E97", {"center": v(0, 30) * mm, "radius": 1.5 * mm});
            skLineSegment(sketch, "E98.bottom", {"start": v(1.5, -38) * mm, "end": v(-1.5, -38) * mm});
            skLineSegment(sketch, "E98.top", {"start": v(1.5, -31) * mm, "end": v(-1.5, -31) * mm});
            skLineSegment(sketch, "E98.left", {"start": v(1.5, -38) * mm, "end": v(1.5, -31) * mm});
            skLineSegment(sketch, "E98.right", {"start": v(-1.5, -38) * mm, "end": v(-1.5, -31) * mm});
            skPoint(sketch, "E98.middle", {"position": v(0, -34.5) * mm});
            skLineSegment(sketch, "E99.bottom", {"start": v(-1.5, 34) * mm, "end": v(1.5, 34) * mm});
            skLineSegment(sketch, "E99.top", {"start": v(-1.5, 41) * mm, "end": v(1.5, 41) * mm});
            skLineSegment(sketch, "E99.left", {"start": v(-1.5, 34) * mm, "end": v(-1.5, 41) * mm});
            skLineSegment(sketch, "E99.right", {"start": v(1.5, 34) * mm, "end": v(1.5, 41) * mm});
            skPoint(sketch, "E99.middle", {"position": v(0, 37.5) * mm});
            skCircle(sketch, "E100.0", {"center": v(0, 1.5) * mm, "radius": 36 * mm, "construction": true});
            skSolve(sketch);
        }
        {
            var Q0;
            Q0 = qSketchRegion(id + "F19", true);
            extrude(context, id + "F20", {"entities" : qUnion([Q0]), "operationType" : NewBodyOperationType.REMOVE, "endBound" : BoundingType.THROUGH_ALL, "oppositeDirection" : true, "depth" : 25 * mm});
        }
        {
            var Q0;
            {var subQ0=sQuery(id+"F14.wireOp",EDGE,"E64");Q0=makeQuery(id+"F20.boolean.opBoolean","COPY",FACE,{"disambiguationData":[TD([makeQuery(id+"F15.opExtrude","SWEPT_FACE",FACE,{"disambiguationData":[OSD([subQ0])]})])],"derivedFrom":makeQuery(id+"F20.opExtrude","SWEPT_FACE",FACE,{"disambiguationData":[OSD([sQuery(id+"F19.wireOp",EDGE,"E99.left")])]})});}
            var sketch = newSketch(context, id + "F21", { "sketchPlane" : qUnion([Q0])});
            skLineSegment(sketch, "E101.0", {"start": v(-65, 34) * mm, "end": v(-65, 37.47) * mm});
            skLineSegment(sketch, "E102.0", {"start": v(-62, 34) * mm, "end": v(-65, 34) * mm});
            skLineSegment(sketch, "E103.0", {"start": v(65, 37.47) * mm, "end": v(65, 34) * mm});
            skLineSegment(sketch, "E103.1", {"start": v(65, 34) * mm, "end": v(62, 34) * mm});
            skLineSegment(sketch, "E104", {"start": v(65, 37.47) * mm, "end": v(-65, 37.47) * mm});
            skLineSegment(sketch, "E105", {"start": v(-62, 34) * mm, "end": v(-62, 31.6) * mm});
            skLineSegment(sketch, "E106", {"start": v(-62, 31.6) * mm, "end": v(-60.5, 31.6) * mm});
            skLineSegment(sketch, "E107", {"start": v(-60.5, 31.6) * mm, "end": v(-60.5, 33) * mm});
            skLineSegment(sketch, "E108", {"start": v(-60.5, 33) * mm, "end": v(-58, 33) * mm});
            skLineSegment(sketch, "E109", {"start": v(-58, 33) * mm, "end": v(-58, 31.6) * mm});
            skLineSegment(sketch, "E110", {"start": v(-58, 31.6) * mm, "end": v(-57, 31.6) * mm});
            skLineSegment(sketch, "E111", {"start": v(-57, 31.6) * mm, "end": v(-57, 28.4) * mm});
            skLineSegment(sketch, "E112", {"start": v(-57, 28.4) * mm, "end": v(-58, 28.4) * mm});
            skLineSegment(sketch, "E113", {"start": v(-58, 28.4) * mm, "end": v(-58, 27) * mm});
            skLineSegment(sketch, "E114", {"start": v(-58, 27) * mm, "end": v(-60.5, 27) * mm});
            skLineSegment(sketch, "E115", {"start": v(-60.5, 27) * mm, "end": v(-60.5, 28.4) * mm});
            skLineSegment(sketch, "E116", {"start": v(-60.5, 28.4) * mm, "end": v(-62, 28.4) * mm});
            skLineSegment(sketch, "E117", {"start": v(-62, 28.4) * mm, "end": v(-62, 24.9) * mm});
            skLineSegment(sketch, "E118", {"start": v(-62, 24.9) * mm, "end": v(62, 24.9) * mm});
            skLineSegment(sketch, "E119.0", {"start": v(-65, 28.5) * mm, "end": v(-65, 31.5) * mm, "construction": true});
            skPoint(sketch, "E120", {"position": v(-65, 30) * mm});
            skPoint(sketch, "E121", {"position": v(-57, 30) * mm});
            skLineSegment(sketch, "E122", {"start": v(-59.25, 33) * mm, "end": v(-59.25, 27) * mm, "construction": true});
            skPoint(sketch, "E123", {"position": v(-59.25, 30) * mm});
            skLineSegment(sketch, "E124", {"start": v(0, 37.47) * mm, "end": v(0, 24.9) * mm, "construction": true});
            skLineSegment(sketch, "E125.MirrorCS", {"start": v(62, 28.4) * mm, "end": v(62, 24.9) * mm});
            skLineSegment(sketch, "E126.MirrorCS", {"start": v(60.5, 28.4) * mm, "end": v(62, 28.4) * mm});
            skLineSegment(sketch, "E127.MirrorCS", {"start": v(60.5, 27) * mm, "end": v(60.5, 28.4) * mm});
            skLineSegment(sketch, "E128.MirrorCS", {"start": v(58, 27) * mm, "end": v(60.5, 27) * mm});
            skLineSegment(sketch, "E129.MirrorCS", {"start": v(58, 28.4) * mm, "end": v(58, 27) * mm});
            skLineSegment(sketch, "E130.MirrorCS", {"start": v(57, 28.4) * mm, "end": v(58, 28.4) * mm});
            skLineSegment(sketch, "E131.MirrorCS", {"start": v(57, 31.6) * mm, "end": v(57, 28.4) * mm});
            skLineSegment(sketch, "E132.MirrorCS", {"start": v(58, 31.6) * mm, "end": v(57, 31.6) * mm});
            skLineSegment(sketch, "E133.MirrorCS", {"start": v(58, 33) * mm, "end": v(58, 31.6) * mm});
            skLineSegment(sketch, "E134.MirrorCS", {"start": v(60.5, 33) * mm, "end": v(58, 33) * mm});
            skLineSegment(sketch, "E135.MirrorCS", {"start": v(60.5, 31.6) * mm, "end": v(60.5, 33) * mm});
            skLineSegment(sketch, "E136.MirrorCS", {"start": v(62, 31.6) * mm, "end": v(60.5, 31.6) * mm});
            skLineSegment(sketch, "E137.MirrorCS", {"start": v(62, 34) * mm, "end": v(62, 31.6) * mm});
            skSolve(sketch);
        }
        {
            var Q0;
            Q0 = qSketchRegion(id + "F21", true);
            extrude(context, id + "F22", {"entities" : qUnion([Q0]), "depth" : 3 * mm});
        }
        {
            var Q0;
            Q0=makeQuery(id+"F15.opExtrude","SWEPT_FACE",FACE,{"disambiguationData":[OSD([sQuery(id+"F14.wireOp",EDGE,"E70.left")])]});
            var sketch = newSketch(context, id + "F23", { "sketchPlane" : qUnion([Q0])});
            skLineSegment(sketch, "E138.0", {"start": v(65, -4.25) * mm, "end": v(62, -4.25) * mm});
            skLineSegment(sketch, "E138.1", {"start": v(62, -4.25) * mm, "end": v(62, -1.25) * mm});
            skLineSegment(sketch, "E138.2", {"start": v(65, -1.25) * mm, "end": v(62, -1.25) * mm});
            skLineSegment(sketch, "E138.3", {"start": v(65, 4.25) * mm, "end": v(62, 4.25) * mm});
            skLineSegment(sketch, "E138.4", {"start": v(62, 7.25) * mm, "end": v(62, 4.25) * mm});
            skLineSegment(sketch, "E138.5", {"start": v(65, 7.25) * mm, "end": v(62, 7.25) * mm});
            skLineSegment(sketch, "E139", {"start": v(65, -1.25) * mm, "end": v(65, 4.25) * mm});
            skLineSegment(sketch, "E140", {"start": v(65, -4.25) * mm, "end": v(75, -4.25) * mm});
            skLineSegment(sketch, "E141", {"start": v(75, -4.25) * mm, "end": v(75, -0.75) * mm});
            skLineSegment(sketch, "E142", {"start": v(75, -0.75) * mm, "end": v(72, -0.75) * mm});
            skLineSegment(sketch, "E143", {"start": v(72, -0.75) * mm, "end": v(72, 3.75) * mm});
            skLineSegment(sketch, "E144", {"start": v(72, 3.75) * mm, "end": v(75, 3.75) * mm});
            skLineSegment(sketch, "E145", {"start": v(75, 3.75) * mm, "end": v(75, 7.25) * mm});
            skLineSegment(sketch, "E146", {"start": v(75, 7.25) * mm, "end": v(65, 7.25) * mm});
            skLineSegment(sketch, "E147", {"start": v(72, 1.5) * mm, "end": v(69.5, 1.5) * mm, "construction": true});
            skLineSegment(sketch, "E148.bottom", {"start": v(72, -0.1) * mm, "end": v(67, -0.1) * mm});
            skLineSegment(sketch, "E148.top", {"start": v(72, 3.1) * mm, "end": v(67, 3.1) * mm});
            skLineSegment(sketch, "E148.left", {"start": v(72, -0.1) * mm, "end": v(72, 3.1) * mm});
            skLineSegment(sketch, "E148.right", {"start": v(67, -0.1) * mm, "end": v(67, 3.1) * mm});
            skPoint(sketch, "E148.middle", {"position": v(69.5, 1.5) * mm});
            skLineSegment(sketch, "E149.bottom", {"start": v(70.75, -1.5) * mm, "end": v(68.25, -1.5) * mm});
            skLineSegment(sketch, "E149.top", {"start": v(70.75, 4.5) * mm, "end": v(68.25, 4.5) * mm});
            skLineSegment(sketch, "E149.left", {"start": v(70.75, -1.5) * mm, "end": v(70.75, 4.5) * mm});
            skLineSegment(sketch, "E149.right", {"start": v(68.25, -1.5) * mm, "end": v(68.25, 4.5) * mm});
            skSolve(sketch);
        }
        {
            var Q0;
            Q0=makeQuery(id+"F23.imprint","IMPRINT",FACE,{"disambiguationData":[TD([[makeQuery(id+"F23.imprint","IMPRINT",EDGE,{"derivedFrom":sQuery(id+"F23.wireOp",EDGE,"E138.3")}),-1.0]])]});
            var Q1;
            Q1=makeQuery(id+"F23.imprint","IMPRINT",FACE,{"disambiguationData":[TD([[makeQuery(id+"F23.imprint","IMPRINT",EDGE,{"derivedFrom":sQuery(id+"F23.wireOp",EDGE,"E138.0")}),-1.0]])]});
            extrude(context, id + "F24", {"entities" : qUnion([Q0, Q1]), "depth" : 3 * mm});
        }
        {
            var Q0;
            Q0=makeQuery(id+"F15.opExtrude","CAP_FACE",FACE,{"disambiguationData":[OSD([sQuery(id+"F14.wireOp",EDGE,"E64"),sQuery(id+"F14.wireOp",EDGE,"E65"),sQuery(id+"F14.wireOp",EDGE,"E66"),sQuery(id+"F14.wireOp",EDGE,"E67"),sQuery(id+"F14.wireOp",EDGE,"E70.bottom"),sQuery(id+"F14.wireOp",EDGE,"E70.top"),sQuery(id+"F14.wireOp",EDGE,"E70.left"),sQuery(id+"F14.wireOp",EDGE,"E70.right"),sQuery(id+"F14.wireOp",EDGE,"E71.MirrorCS"),sQuery(id+"F14.wireOp",EDGE,"E72.MirrorCS"),sQuery(id+"F14.wireOp",EDGE,"E73.MirrorCS"),sQuery(id+"F14.wireOp",EDGE,"E74.MirrorCS"),sQuery(id+"F14.wireOp",EDGE,"E76.MirrorCS"),sQuery(id+"F14.wireOp",EDGE,"E77.MirrorCS"),sQuery(id+"F14.wireOp",EDGE,"E78.MirrorCS"),sQuery(id+"F14.wireOp",EDGE,"E79.MirrorCS"),sQuery(id+"F14.wireOp",EDGE,"E80.MirrorCS"),sQuery(id+"F14.wireOp",EDGE,"E81.MirrorCS"),sQuery(id+"F14.wireOp",EDGE,"E82.MirrorCS"),sQuery(id+"F14.wireOp",EDGE,"E83.MirrorCS"),sQuery(id+"F14.wireOp",EDGE,"E84"),sQuery(id+"F14.wireOp",EDGE,"E85"),sQuery(id+"F14.wireOp",EDGE,"E86"),sQuery(id+"F14.wireOp",EDGE,"E88.0.0"),sQuery(id+"F14.wireOp",EDGE,"E88.0.1"),sQuery(id+"F14.wireOp",EDGE,"E88.0.2"),sQuery(id+"F14.wireOp",EDGE,"E88.0.3"),sQuery(id+"F14.wireOp",EDGE,"E88.1.0"),sQuery(id+"F14.wireOp",EDGE,"E88.1.1"),sQuery(id+"F14.wireOp",EDGE,"E88.1.2"),sQuery(id+"F14.wireOp",EDGE,"E88.1.3")])],"isStart":false});
            cPlane(context, id + "F25", {"entities" : qUnion([Q0]), "cplaneType" : CPlaneType.OFFSET, "offset" : 50 * mm, "width" : 150 * mm, "height" : 150 * mm});
        }
        {
            var Q0;
            Q0=qCreatedBy(id+"F25.planeOp",FACE);
            var sketch = newSketch(context, id + "F26", { "sketchPlane" : qUnion([Q0])});
            skArc(sketch, "E150.0", {"start": v(1.5, -34.47) * mm, "mid": v(36, 1.5) * mm, "end": v(1.5, 37.47) * mm, "construction": true});
            skCircle(sketch, "E151", {"center": v(0, 1.5) * mm, "radius": 26.5 * mm});
            skLineSegment(sketch, "E152.0", {"start": v(-24.5, -4.25) * mm, "end": v(-21.5, -4.25) * mm});
            skLineSegment(sketch, "E152.1", {"start": v(-21.5, -4.25) * mm, "end": v(-21.5, -1.25) * mm});
            skLineSegment(sketch, "E152.2", {"start": v(-24.5, -1.25) * mm, "end": v(-21.5, -1.25) * mm});
            skLineSegment(sketch, "E152.3", {"start": v(-24.5, -4.25) * mm, "end": v(-24.5, -1.25) * mm});
            skLineSegment(sketch, "E152.4", {"start": v(-24.5, 4.25) * mm, "end": v(-21.5, 4.25) * mm});
            skLineSegment(sketch, "E152.5", {"start": v(-21.5, 7.25) * mm, "end": v(-21.5, 4.25) * mm});
            skLineSegment(sketch, "E152.6", {"start": v(-24.5, 7.25) * mm, "end": v(-21.5, 7.25) * mm});
            skLineSegment(sketch, "E152.7", {"start": v(-24.5, 7.25) * mm, "end": v(-24.5, 4.25) * mm});
            skLineSegment(sketch, "E153", {"start": v(0, 1.5) * mm, "end": v(0, -11.93) * mm, "construction": true});
            skLineSegment(sketch, "E154.MirrorCS", {"start": v(24.5, -4.25) * mm, "end": v(21.5, -4.25) * mm});
            skLineSegment(sketch, "E155.MirrorCS", {"start": v(21.5, -4.25) * mm, "end": v(21.5, -1.25) * mm});
            skLineSegment(sketch, "E156.MirrorCS", {"start": v(24.5, -1.25) * mm, "end": v(21.5, -1.25) * mm});
            skLineSegment(sketch, "E157.MirrorCS", {"start": v(24.5, -4.25) * mm, "end": v(24.5, -1.25) * mm});
            skLineSegment(sketch, "E158.MirrorCS", {"start": v(24.5, 4.25) * mm, "end": v(21.5, 4.25) * mm});
            skLineSegment(sketch, "E159.MirrorCS", {"start": v(21.5, 7.25) * mm, "end": v(21.5, 4.25) * mm});
            skLineSegment(sketch, "E160.MirrorCS", {"start": v(24.5, 7.25) * mm, "end": v(21.5, 7.25) * mm});
            skLineSegment(sketch, "E161.MirrorCS", {"start": v(24.5, 7.25) * mm, "end": v(24.5, 4.25) * mm});
            skLineSegment(sketch, "E162", {"start": v(-23, -1.25) * mm, "end": v(-23, 4.25) * mm, "construction": true});
            skLineSegment(sketch, "E163", {"start": v(23, -1.25) * mm, "end": v(23, 4.25) * mm, "construction": true});
            skCircle(sketch, "E164", {"center": v(23, 1.5) * mm, "radius": 1.5 * mm});
            skCircle(sketch, "E165.MirrorC", {"center": v(-23, 1.5) * mm, "radius": 1.5 * mm});
            skLineSegment(sketch, "E166.bottom", {"start": v(4, -2.5) * mm, "end": v(-4, -2.5) * mm, "construction": true});
            skLineSegment(sketch, "E166.top", {"start": v(4, 5.5) * mm, "end": v(-4, 5.5) * mm, "construction": true});
            skLineSegment(sketch, "E166.left", {"start": v(4, -2.5) * mm, "end": v(4, 5.5) * mm, "construction": true});
            skLineSegment(sketch, "E166.right", {"start": v(-4, -2.5) * mm, "end": v(-4, 5.5) * mm, "construction": true});
            skLineSegment(sketch, "E167.bottom", {"start": v(6, -14) * mm, "end": v(-6, -14) * mm});
            skLineSegment(sketch, "E167.top", {"start": v(6, 8.5) * mm, "end": v(-6, 8.5) * mm});
            skLineSegment(sketch, "E167.left", {"start": v(6, -14) * mm, "end": v(6, 8.5) * mm});
            skLineSegment(sketch, "E167.right", {"start": v(-6, -14) * mm, "end": v(-6, 8.5) * mm});
            skPoint(sketch, "E167.middle", {"position": v(0, -2.75) * mm});
            skCircle(sketch, "E168", {"center": v(10.5, 1.5) * mm, "radius": 1.25 * mm});
            skCircle(sketch, "E169", {"center": v(10.5, -11) * mm, "radius": 1.25 * mm});
            skCircle(sketch, "E170", {"center": v(-10.5, -11) * mm, "radius": 1.25 * mm});
            skCircle(sketch, "E171", {"center": v(-10.5, 1.5) * mm, "radius": 1.25 * mm});
            skLineSegment(sketch, "E172", {"start": v(10.5, 1.5) * mm, "end": v(-10.5, 1.5) * mm, "construction": true});
            skSolve(sketch);
        }
        {
            var Q0;
            Q0 = qSketchRegion(id + "F26", true);
            extrude(context, id + "F27", {"entities" : qUnion([Q0]), "depth" : 3 * mm});
        }
        {
            var Q0;
            Q0=makeQuery(id+"F1.opExtrude","CAP_FACE",FACE,{"disambiguationData":[OSD([sQuery(id+"F0.wireOp",EDGE,"E0.bottom"),sQuery(id+"F0.wireOp",EDGE,"E0.top"),sQuery(id+"F0.wireOp",EDGE,"E0.left"),sQuery(id+"F0.wireOp",EDGE,"E0.right"),sQuery(id+"F0.wireOp",EDGE,"E3.bottom"),sQuery(id+"F0.wireOp",EDGE,"E3.top"),sQuery(id+"F0.wireOp",EDGE,"E3.right"),sQuery(id+"F0.wireOp",EDGE,"E4.MirrorCS"),sQuery(id+"F0.wireOp",EDGE,"E5.MirrorCS"),sQuery(id+"F0.wireOp",EDGE,"E6.MirrorCS"),sQuery(id+"F0.wireOp",EDGE,"E7.MirrorCS"),sQuery(id+"F0.wireOp",EDGE,"E8.MirrorCS"),sQuery(id+"F0.wireOp",EDGE,"E9.MirrorCS"),sQuery(id+"F0.wireOp",EDGE,"E10.MirrorCS"),sQuery(id+"F0.wireOp",EDGE,"E11.MirrorCS"),sQuery(id+"F0.wireOp",EDGE,"E12.MirrorCS")])],"isStart":true});
            var sketch = newSketch(context, id + "F28", { "sketchPlane" : qUnion([Q0])});
            skCircle(sketch, "E173", {"center": v(55.5, -30.5) * mm, "radius": 1.52 * mm});
            skCircle(sketch, "E174", {"center": v(-57.5, -30.5) * mm, "radius": 1.52 * mm});
            skCircle(sketch, "E175", {"center": v(-57.5, 30.5) * mm, "radius": 1.52 * mm});
            skCircle(sketch, "E176", {"center": v(55.5, 30.5) * mm, "radius": 1.52 * mm});
            skSolve(sketch);
        }
        {
            var Q0;
            Q0 = qSketchRegion(id + "F28", true);
            extrude(context, id + "F29", {"entities" : qUnion([Q0]), "operationType" : NewBodyOperationType.REMOVE, "oppositeDirection" : true, "depth" : 25 * mm});
        }
    });
